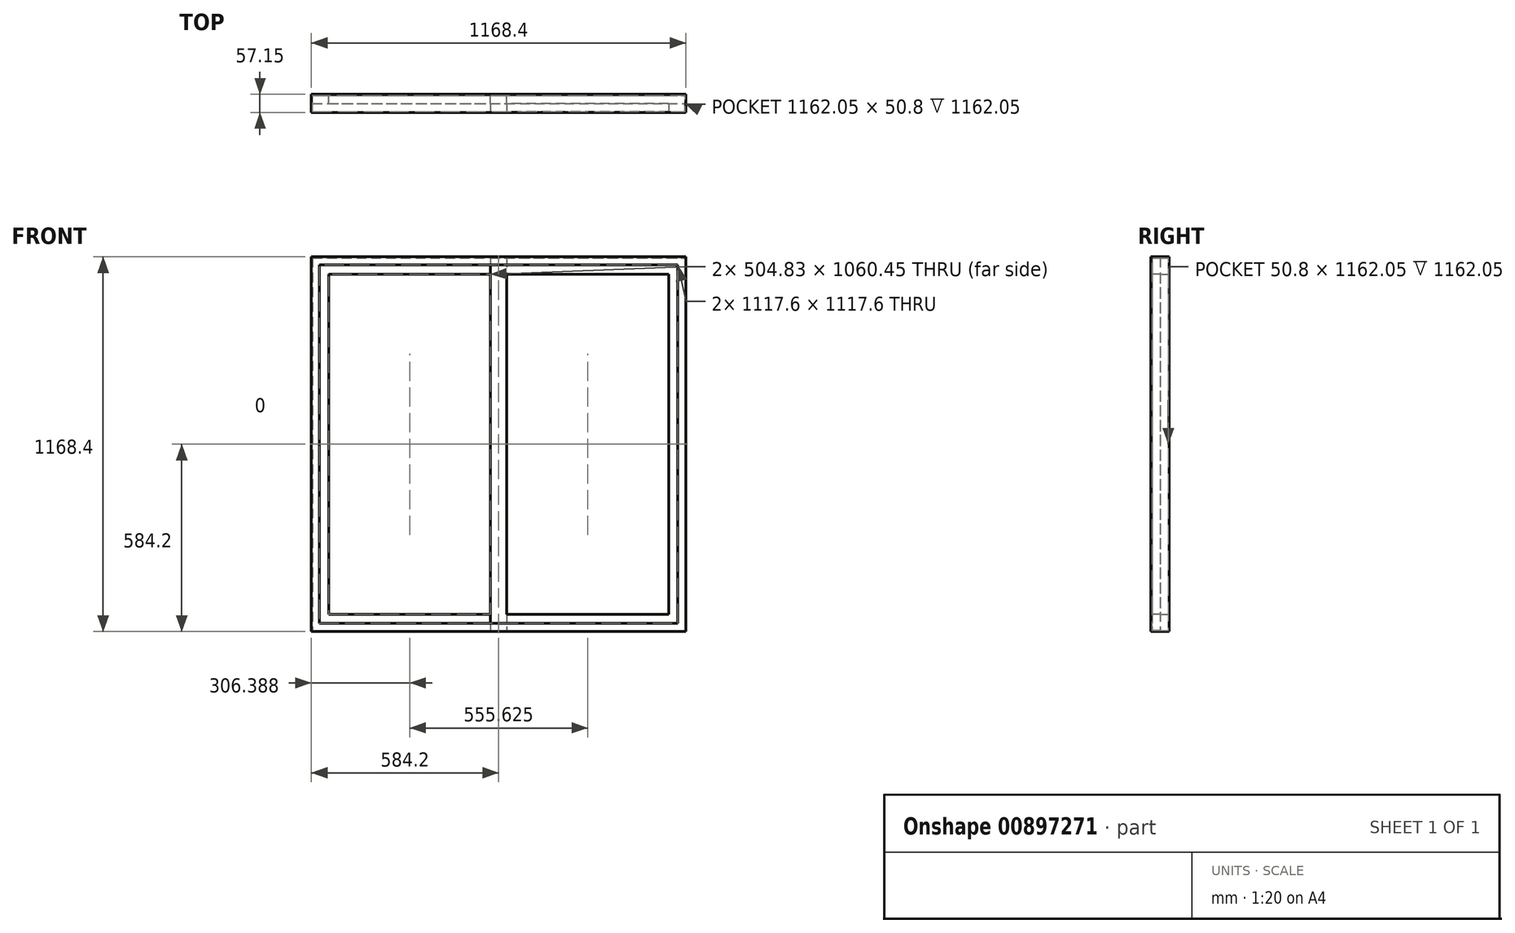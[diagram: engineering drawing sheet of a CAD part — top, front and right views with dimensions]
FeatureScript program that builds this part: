
annotation { "Feature Type Name" : "Feature", "Feature Type Description" : "" }
export const myFeature = defineFeature(function(context is Context, id is Id, definition is map)
    precondition{}
    {
        {
            var Q0;
            Q0=qCreatedBy(makeId("Front.planeOp"),FACE);
            var sketch = newSketch(context, id + "F0", { "sketchPlane" : qUnion([Q0])});
            skLineSegment(sketch, "E0.bottom", {"start": v(-584.2, 584.2) * mm, "end": v(584.2, 584.2) * mm});
            skLineSegment(sketch, "E0.top", {"start": v(-584.2, -584.2) * mm, "end": v(584.2, -584.2) * mm});
            skLineSegment(sketch, "E0.left", {"start": v(-584.2, 584.2) * mm, "end": v(-584.2, -584.2) * mm});
            skLineSegment(sketch, "E0.right", {"start": v(584.2, 584.2) * mm, "end": v(584.2, -584.2) * mm});
            skPoint(sketch, "E0.middle", {"position": v(0, 0) * mm});
            skLineSegment(sketch, "E1.0", {"start": v(-558.8, 558.8) * mm, "end": v(558.8, 558.8) * mm});
            skLineSegment(sketch, "E1.1", {"start": v(-558.8, 558.8) * mm, "end": v(-558.8, -558.8) * mm});
            skLineSegment(sketch, "E1.2", {"start": v(-558.8, -558.8) * mm, "end": v(558.8, -558.8) * mm});
            skLineSegment(sketch, "E1.3", {"start": v(558.8, 558.8) * mm, "end": v(558.8, -558.8) * mm});
            skSolve(sketch);
        }
        {
            var Q0;
            Q0=makeQuery(id+"F0.imprint","IMPRINT",FACE,{"disambiguationData":[TD([[makeQuery(id+"F0.imprint","IMPRINT",EDGE,{"derivedFrom":sQuery(id+"F0.wireOp",EDGE,"E0.bottom")}),-1.0]])]});
            extrude(context, id + "F1", {"entities" : qUnion([Q0]), "depth" : 57.15 * mm, "offsetDistance" : 25.4 * mm});
        }
        {
            var Q0;
            Q0=makeQuery(id+"F1.opExtrude","SWEPT_FACE",FACE,{"disambiguationData":[OSD([sQuery(id+"F0.wireOp",EDGE,"E1.3")])]});
            var Q1;
            Q1=makeQuery(id+"F1.opExtrude","SWEPT_FACE",FACE,{"disambiguationData":[OSD([sQuery(id+"F0.wireOp",EDGE,"E1.0")])]});
            var Q2;
            Q2=makeQuery(id+"F1.opExtrude","SWEPT_FACE",FACE,{"disambiguationData":[OSD([sQuery(id+"F0.wireOp",EDGE,"E1.1")])]});
            var Q3;
            Q3=makeQuery(id+"F1.opExtrude","SWEPT_FACE",FACE,{"disambiguationData":[OSD([sQuery(id+"F0.wireOp",EDGE,"E1.2")])]});
            shell(context, id + "F2", {"entities" : qUnion([Q0, Q1, Q2, Q3]), "thickness" : 3.17 * mm});
        }
        {
            var Q0;
            {var subQ0=sQuery(id+"F0.wireOp",EDGE,"E1.3");var subQ1=sQuery(id+"F0.wireOp",EDGE,"E1.2");var subQ2=sQuery(id+"F0.wireOp",EDGE,"E1.1");var subQ3=sQuery(id+"F0.wireOp",EDGE,"E1.0");var subQ4=sQuery(id+"F0.wireOp",EDGE,"E0.right");var subQ5=sQuery(id+"F0.wireOp",EDGE,"E0.left");var subQ6=sQuery(id+"F0.wireOp",EDGE,"E0.top");var subQ7=sQuery(id+"F0.wireOp",EDGE,"E0.bottom");Q0=makeQuery(id+"F2.opShell","OFFSET_FACE",FACE,{"disambiguationData":[OSD([subQ7,subQ6,subQ5,subQ4,subQ3,subQ2,subQ1,subQ0]),TDD([makeQuery(id+"F1.opExtrude","CAP_FACE",FACE,{"disambiguationData":[OSD([subQ7,subQ6,subQ5,subQ4,subQ3,subQ2,subQ1,subQ0])],"isStart":true})])]});}
            var sketch = newSketch(context, id + "F3", { "sketchPlane" : qUnion([Q0])});
            skLineSegment(sketch, "E2", {"start": v(0, -581.02) * mm, "end": v(0, 581.03) * mm, "construction": true});
            skLineSegment(sketch, "E3.bottom", {"start": v(-581.02, 581.03) * mm, "end": v(25.4, 581.03) * mm});
            skLineSegment(sketch, "E3.top", {"start": v(-581.02, -581.02) * mm, "end": v(25.4, -581.02) * mm});
            skLineSegment(sketch, "E3.left", {"start": v(-581.02, 581.03) * mm, "end": v(-581.02, -581.02) * mm});
            skLineSegment(sketch, "E3.right", {"start": v(25.4, 581.03) * mm, "end": v(25.4, -581.02) * mm});
            skLineSegment(sketch, "E4.0", {"start": v(-530.22, 530.23) * mm, "end": v(-25.4, 530.23) * mm});
            skLineSegment(sketch, "E4.1", {"start": v(-530.22, 530.23) * mm, "end": v(-530.22, -530.23) * mm});
            skLineSegment(sketch, "E4.2", {"start": v(-530.22, -530.23) * mm, "end": v(-25.4, -530.23) * mm});
            skLineSegment(sketch, "E4.3", {"start": v(-25.4, 530.23) * mm, "end": v(-25.4, -530.23) * mm});
            skSolve(sketch);
        }
        {
            var Q0;
            {var subQ1=sQuery(id+"F3.wireOp",EDGE,"E3.bottom");Q0=makeQuery(id+"F3.imprint","IMPRINT",FACE,{"disambiguationData":[TD([[makeQuery(id+"F3.imprint","IMPRINT",EDGE,{"derivedFrom":subQ1}),-1.0]])]});}
            var Q1;
            Q1=makeQuery(id+"F3.imprint","IMPRINT",FACE,{"disambiguationData":[TD([[makeQuery(id+"F3.imprint","IMPRINT",EDGE,{"derivedFrom":sQuery(id+"F3.wireOp",EDGE,"E4.0")}),1.0]])]});
            extrude(context, id + "F4", {"entities" : qUnion([Q0, Q1]), "depth" : 25.4 * mm, "offsetDistance" : 25.4 * mm});
        }
        {
            var Q0;
            {var subQ0=sQuery(id+"F0.wireOp",EDGE,"E1.3");var subQ1=sQuery(id+"F0.wireOp",EDGE,"E1.2");var subQ2=sQuery(id+"F0.wireOp",EDGE,"E1.1");var subQ3=sQuery(id+"F0.wireOp",EDGE,"E1.0");var subQ4=sQuery(id+"F0.wireOp",EDGE,"E0.right");var subQ5=sQuery(id+"F0.wireOp",EDGE,"E0.left");var subQ6=sQuery(id+"F0.wireOp",EDGE,"E0.top");var subQ7=sQuery(id+"F0.wireOp",EDGE,"E0.bottom");Q0=makeQuery(id+"F2.opShell","OFFSET_FACE",FACE,{"disambiguationData":[OSD([subQ7,subQ6,subQ5,subQ4,subQ3,subQ2,subQ1,subQ0]),TDD([makeQuery(id+"F1.opExtrude","CAP_FACE",FACE,{"disambiguationData":[OSD([subQ7,subQ6,subQ5,subQ4,subQ3,subQ2,subQ1,subQ0])],"isStart":false})])]});}
            var sketch = newSketch(context, id + "F5", { "sketchPlane" : qUnion([Q0])});
            skLineSegment(sketch, "E5.bottom", {"start": v(-581.03, 581.03) * mm, "end": v(25.4, 581.03) * mm});
            skLineSegment(sketch, "E5.top", {"start": v(-581.03, -581.02) * mm, "end": v(25.4, -581.02) * mm});
            skLineSegment(sketch, "E5.left", {"start": v(-581.03, 581.03) * mm, "end": v(-581.03, -581.02) * mm});
            skLineSegment(sketch, "E5.right", {"start": v(25.4, 581.03) * mm, "end": v(25.4, -581.02) * mm});
            skLineSegment(sketch, "E6.0", {"start": v(-530.23, 530.23) * mm, "end": v(-530.23, -530.23) * mm});
            skLineSegment(sketch, "E6.1", {"start": v(-530.23, 530.23) * mm, "end": v(-25.4, 530.23) * mm});
            skLineSegment(sketch, "E6.2", {"start": v(-25.4, 530.23) * mm, "end": v(-25.4, -530.23) * mm});
            skLineSegment(sketch, "E6.3", {"start": v(-530.23, -530.23) * mm, "end": v(-25.4, -530.23) * mm});
            skSolve(sketch);
        }
        {
            var Q0;
            Q0=makeQuery(id+"F5.imprint","IMPRINT",FACE,{"disambiguationData":[TD([[makeQuery(id+"F5.imprint","IMPRINT",EDGE,{"derivedFrom":sQuery(id+"F5.wireOp",EDGE,"E6.0")}),-1.0]])]});
            var Q1;
            {var subQ1=sQuery(id+"F5.wireOp",EDGE,"E5.bottom");Q1=makeQuery(id+"F5.imprint","IMPRINT",FACE,{"disambiguationData":[TD([[makeQuery(id+"F5.imprint","IMPRINT",EDGE,{"derivedFrom":subQ1}),1.0]])]});}
            extrude(context, id + "F6", {"entities" : qUnion([Q0, Q1]), "depth" : 25.4 * mm, "offsetDistance" : 25.4 * mm});
        }
        {
            var Q0;
            Q0=makeQuery(id+"F3.imprint","IMPRINT",FACE,{"disambiguationData":[TD([[makeQuery(id+"F3.imprint","IMPRINT",EDGE,{"derivedFrom":sQuery(id+"F3.wireOp",EDGE,"E4.0")}),-1.0]])]});
            extrude(context, id + "F7", {"entities" : qUnion([Q0]), "depth" : 25.4 * mm, "offsetDistance" : 25.4 * mm});
        }
        {
            var Q0;
            Q0=makeQuery(id+"F5.imprint","IMPRINT",FACE,{"disambiguationData":[TD([[makeQuery(id+"F5.imprint","IMPRINT",EDGE,{"derivedFrom":sQuery(id+"F5.wireOp",EDGE,"E6.0")}),1.0]])]});
            extrude(context, id + "F8", {"entities" : qUnion([Q0]), "depth" : 25.4 * mm, "offsetDistance" : 25.4 * mm});
        }
    });
